# Revit family: Sanitary_Showers_AXOR_10625CHN-AXOR-ShowerSolutions-ShowerHeav_new
name_source: partatom
category: Plumbing Fixtures
units: mm (PartAtom-declared; Revit-internal decimal feet)

## family parameters
Cut with Voids When Loaded = Yes
Host = Face
OmniClass Number = 23.31.17.00
OmniClass Title = Showers
Part Type = Normal
Room Calculation Point = No
Round Connector Dimension = Use Diameter
Shared = No

## types (1)
- 807 Chrome
    Connector Description = Water Inlet 19.1mm
    Default Elevation = 1219 mm
    Description = AXOR ShowerSolutions ShowerHeaven 720/720 3jet without lighting
    Diameter = 19 mm
    Manufacturer = AXOR
    Material = AXOR - Metal - 807 Chrome
    Model = 10625CHN
    Product Guid = 52709c04-78ef-4523-81c6-8667269e62d7
    Product Page URL = https://www.axor-design.com
    Product data url = https://bimobject.com
    URL = https://www.axor-design.com
    Version = 1

## geometry (parser evidence)
native form markers: Sweep x2
no freeform markers — native parametric forms only
